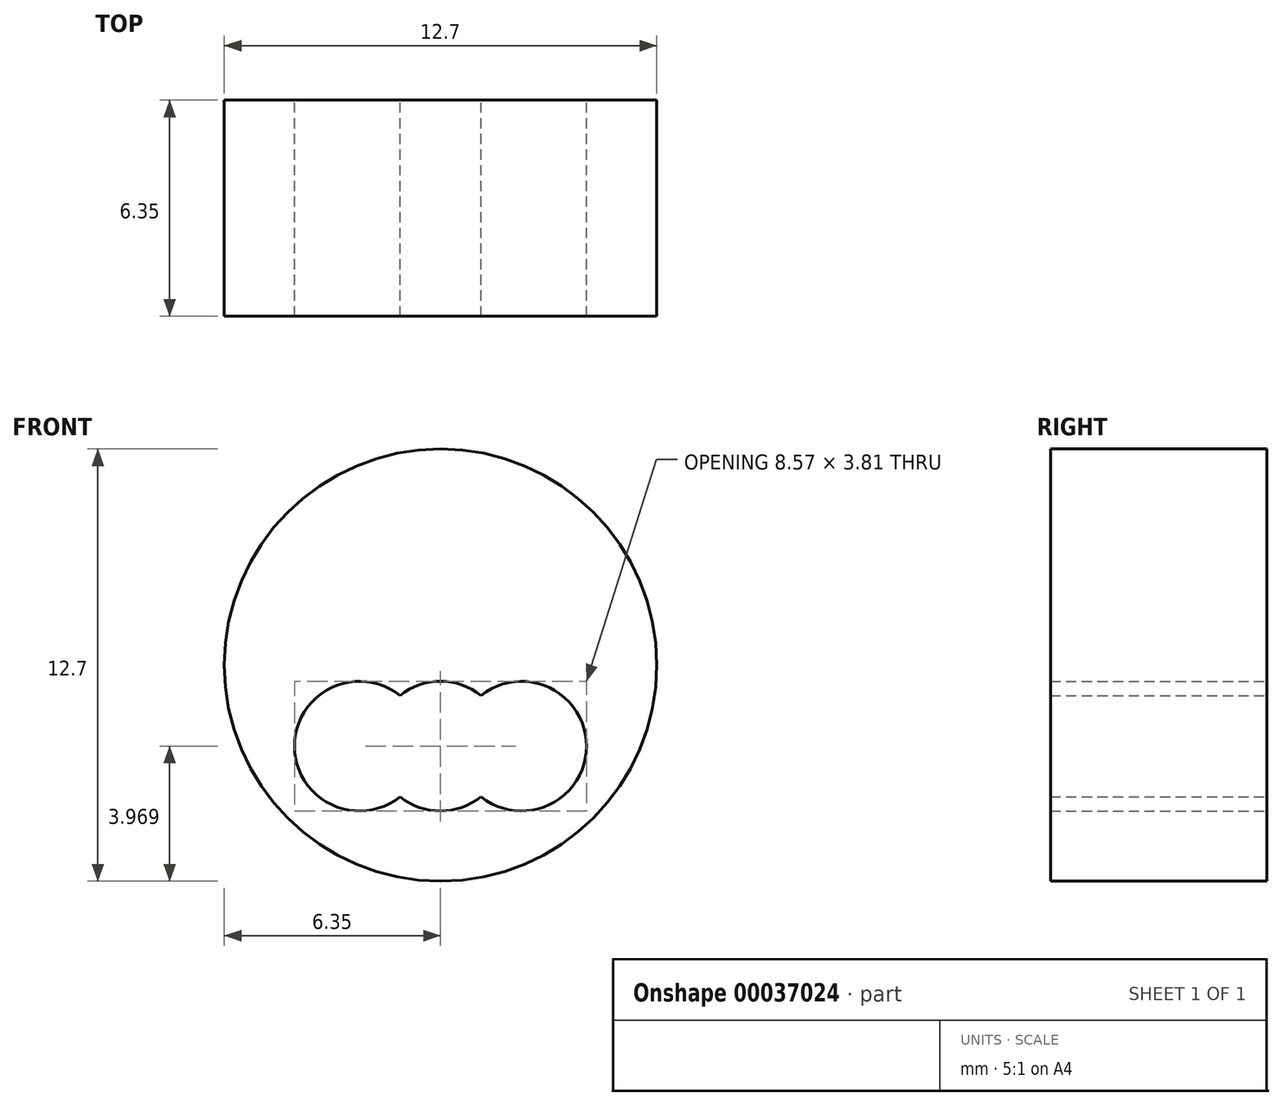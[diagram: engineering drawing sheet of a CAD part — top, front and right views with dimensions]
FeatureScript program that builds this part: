
annotation { "Feature Type Name" : "Feature", "Feature Type Description" : "" }
export const myFeature = defineFeature(function(context is Context, id is Id, definition is map)
    precondition{}
    {
        {
            var Q0;
            Q0=qCreatedBy(makeId("Front.planeOp"),FACE);
            var sketch = newSketch(context, id + "F0", { "sketchPlane" : qUnion([Q0])});
            skCircle(sketch, "E0", {"center": v(0, 0) * mm, "radius": 6.35 * mm});
            skLineSegment(sketch, "E1", {"start": v(0, -2.38) * mm, "end": v(0, 2.38) * mm, "construction": true});
            skLineSegment(sketch, "E2", {"start": v(-2.38, -2.38) * mm, "end": v(2.38, -2.38) * mm, "construction": true});
            skPoint(sketch, "E3", {"position": v(0, -2.38) * mm});
            skSolve(sketch);
        }
        {
            var Q0;
            Q0=makeQuery(id+"F0.imprint","IMPRINT",FACE,{"disambiguationData":[TD([[makeQuery(id+"F0.imprint","IMPRINT",EDGE,{"derivedFrom":sQuery(id+"F0.wireOp",EDGE,"E0")}),1.0]])]});
            extrude(context, id + "F1", {"entities" : qUnion([Q0]), "depth" : 6.35 * mm});
        }
        {
            var Q0;
            Q0=sQuery(id+"F0.wireOp",VERTEX,"E2.end");
            var Q1;
            Q1=sQuery(id+"F0.wireOp",VERTEX,"E1.start");
            var Q2;
            Q2=sQuery(id+"F0.wireOp",VERTEX,"E2.start");
            var Q3;
            Q3=makeQuery(id+"F1.opExtrude","SWEPT_BODY",BODY,{"disambiguationData":[OSD([sQuery(id+"F0.wireOp",EDGE,"E0")])]});
            hole(context, id + "F2", {"style" : HoleStyle.SIMPLE, "holeDiameter" : 3.8 * mm, "endStyle" : HoleEndStyle.THROUGH, "oppositeDirection" : true, "locations" : qUnion([Q0, Q1, Q2]), "scope" : qUnion([Q3])});
        }
    });
